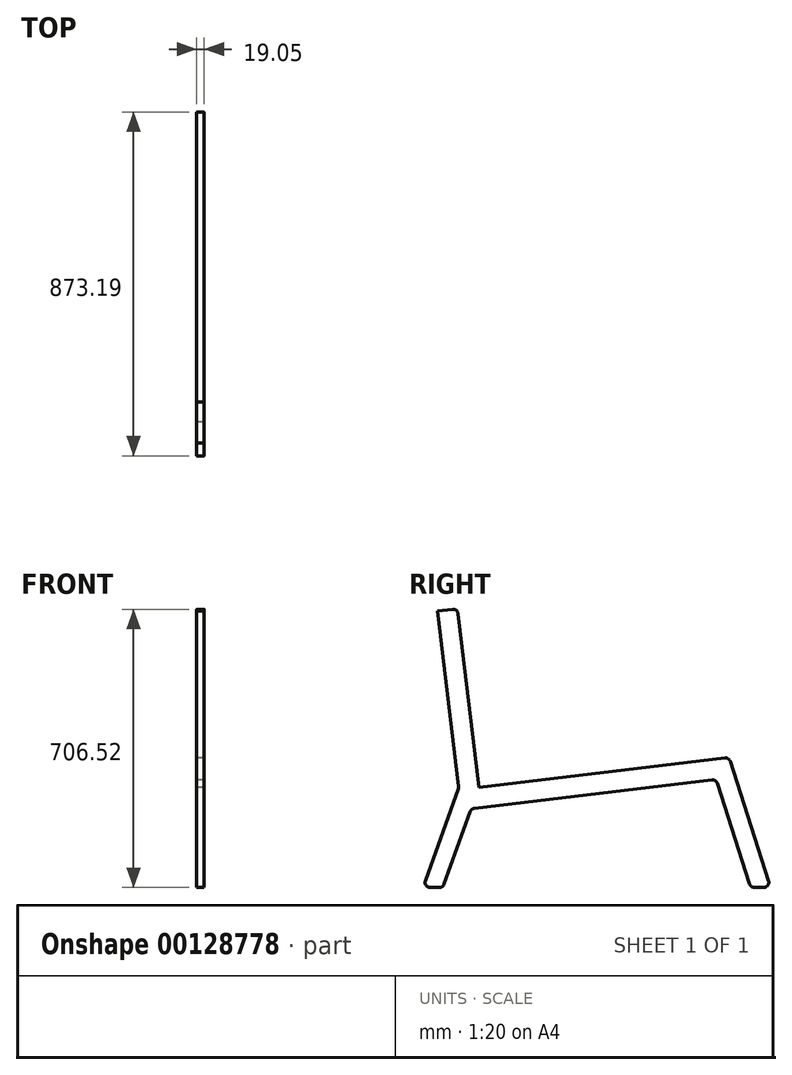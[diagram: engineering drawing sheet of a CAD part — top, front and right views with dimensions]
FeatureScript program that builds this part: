
annotation { "Feature Type Name" : "Feature", "Feature Type Description" : "" }
export const myFeature = defineFeature(function(context is Context, id is Id, definition is map)
    precondition{}
    {
        {
            var Q0;
            Q0=qCreatedBy(makeId("Right.planeOp"),FACE);
            var sketch = newSketch(context, id + "F0", { "sketchPlane" : qUnion([Q0])});
            skLineSegment(sketch, "E0", {"start": v(0, 0) * mm, "end": v(0, -254) * mm, "construction": true});
            skLineSegment(sketch, "E1", {"start": v(0, -254) * mm, "end": v(635, -254) * mm, "construction": true});
            skLineSegment(sketch, "E2", {"start": v(635, -254) * mm, "end": v(635, 76.2) * mm, "construction": true});
            skLineSegment(sketch, "E3", {"start": v(0, 0) * mm, "end": v(635, 76.2) * mm, "construction": true});
            skLineSegment(sketch, "E4", {"start": v(0, 0) * mm, "end": v(-54.47, 453.94) * mm, "construction": true});
            skLineSegment(sketch, "E5", {"start": v(638.2, 66.22) * mm, "end": v(735.58, -237.42) * mm});
            skLineSegment(sketch, "E6", {"start": v(-52.96, 441.33) * mm, "end": v(0, 0) * mm});
            skLineSegment(sketch, "E7", {"start": v(624.6, 74.95) * mm, "end": v(0, 0) * mm});
            skLineSegment(sketch, "E8", {"start": v(-67.08, 452.43) * mm, "end": v(-104.91, 447.9) * mm});
            skLineSegment(sketch, "E9", {"start": v(-104.91, 447.9) * mm, "end": v(-51.52, 2.98) * mm});
            skLineSegment(sketch, "E10", {"start": v(-52.18, -2.82) * mm, "end": v(-136.26, -237) * mm});
            skLineSegment(sketch, "E11", {"start": v(-124.3, -254) * mm, "end": v(-100.5, -254) * mm});
            skLineSegment(sketch, "E12", {"start": v(-88.54, -245.6) * mm, "end": v(-22.53, -61.73) * mm});
            skLineSegment(sketch, "E13", {"start": v(-12.09, -53.4) * mm, "end": v(591.72, 19.05) * mm});
            skLineSegment(sketch, "E14", {"start": v(605.33, 10.32) * mm, "end": v(687.26, -245.18) * mm});
            skLineSegment(sketch, "E15", {"start": v(723.48, -254) * mm, "end": v(699.36, -254) * mm});
            skLineSegment(sketch, "E16", {"start": v(-91.56, -254) * mm, "end": v(0, -254) * mm, "construction": true});
            skLineSegment(sketch, "E17", {"start": v(690.1, -254) * mm, "end": v(635, -254) * mm, "construction": true});
            skPoint(sketch, "E18.visualSharp", {"position": v(635, 76.2) * mm});
            skArc(sketch, "E18.filletArc", {"start": v(638.2, 66.22) * mm, "mid": v(632.97, 73.03) * mm, "end": v(624.6, 74.95) * mm});
            skPoint(sketch, "E19.visualSharp", {"position": v(740.9, -254) * mm});
            skArc(sketch, "E19.filletArc", {"start": v(723.48, -254) * mm, "mid": v(733.74, -248.78) * mm, "end": v(735.58, -237.42) * mm});
            skPoint(sketch, "E20.visualSharp", {"position": v(690.1, -254) * mm});
            skArc(sketch, "E20.filletArc", {"start": v(687.26, -245.18) * mm, "mid": v(691.87, -251.56) * mm, "end": v(699.36, -254) * mm});
            skPoint(sketch, "E21.visualSharp", {"position": v(602.13, 20.3) * mm});
            skArc(sketch, "E21.filletArc", {"start": v(605.33, 10.32) * mm, "mid": v(600.1, 17.13) * mm, "end": v(591.72, 19.05) * mm});
            skPoint(sketch, "E22.visualSharp", {"position": v(-19.88, -54.34) * mm});
            skArc(sketch, "E22.filletArc", {"start": v(-12.09, -53.4) * mm, "mid": v(-18.49, -56.09) * mm, "end": v(-22.53, -61.73) * mm});
            skPoint(sketch, "E23.visualSharp", {"position": v(-91.56, -254) * mm});
            skArc(sketch, "E23.filletArc", {"start": v(-100.5, -254) * mm, "mid": v(-93.19, -251.69) * mm, "end": v(-88.54, -245.6) * mm});
            skPoint(sketch, "E24.visualSharp", {"position": v(-142.36, -254) * mm});
            skArc(sketch, "E24.filletArc", {"start": v(-136.26, -237) * mm, "mid": v(-134.7, -248.6) * mm, "end": v(-124.3, -254) * mm});
            skPoint(sketch, "E25.visualSharp", {"position": v(-51.16, 0) * mm});
            skArc(sketch, "E25.filletArc", {"start": v(-52.18, -2.82) * mm, "mid": v(-51.51, 0.04) * mm, "end": v(-51.52, 2.98) * mm});
            skPoint(sketch, "E26.visualSharp", {"position": v(-54.47, 453.94) * mm});
            skArc(sketch, "E26.filletArc", {"start": v(-52.96, 441.33) * mm, "mid": v(-57.72, 449.8) * mm, "end": v(-67.08, 452.43) * mm});
            skSolve(sketch);
        }
        {
            var Q0;
            Q0 = qSketchRegion(id + "F0", true);
            extrude(context, id + "F1", {"entities" : qUnion([Q0]), "depth" : 19.05 * mm});
        }
    });
